# Revit family: JOMA_437
name_source: partatom
category: Structural Connections
revit_build: Autodesk Revit 2017 (Build: 20171027_0315(x64)
units: mm (PartAtom-declared; Revit-internal decimal feet)

## family parameters
Cut with Voids When Loaded = No
Enable cutting in views = Yes
Host = Face
Material for Model Behavior = Other
Shared = No

## types (7) — shared parameters
Default Elevation = 1200 mm
Länk Joma Dimensioneringsverktyg = http://www.joma.se
Material = Varmförzinkad stålplåt
t = 3 mm  [stored 0.00984252 ft]

## per-type parameters (varying)
| type | Beslag 4370001 | Beslag 4370002 | Beslag 4370003 | Beslag 4370004 | Förstärkningsbricka | Förstärkningsbricka 3012002 3D | Förstärkningsbricka 3012003 3D | Typ | Typ Förstärkningsbricka | Vikt (kg) | b | h | l |
| 4370001 | Yes | No | No | No | No | No | No | VINKEL 4370001 |  | 1,15 | 93 mm | 120 mm | 240 mm |
| 4370002 | No | Yes | No | No | No | No | No | VINKEL 4370002 |  | 1,04 | 103 mm | 120 mm | 200 mm |
| 4370003 | No | No | Yes | No | No | No | No | VINKEL 4370003 |  | 1,04 | 123 mm | 120 mm | 240 mm |
| 4370004 | No | No | No | Yes | No | No | No | VINKEL 4370004 |  | 0,78 | 103 mm | 71 mm | 200 mm |
| 4370002 med 3012002 | No | Yes | No | No | Yes | Yes | No | VINKEL 4370002 | FÖRSTÄRKNINGSBRICKA 3012002 | 1,04 + 1,33 | 103 mm | 120 mm | 200 mm |
| 4370004 med 3012002 | No | No | No | Yes | Yes | Yes | No | VINKEL 4370004 | FÖRSTÄRKNINGSBRICKA 3012002 | 0,78 + 1,33 | 103 mm | 71 mm | 200 mm |
| 4370003 med 3012003 | No | No | Yes | No | Yes | No | Yes | VINKEL 4370003 | FÖRSTÄRKNINGSBRICKA 3012003 | 1,04 + 1,62 | 123 mm | 120 mm | 240 mm |

note: [stored X ft] marks values corroborated as IEEE doubles in the binary element streams (Revit-internal decimal feet)

## geometry (parser evidence)
native form markers: Sweep x9
no freeform markers — native parametric forms only
